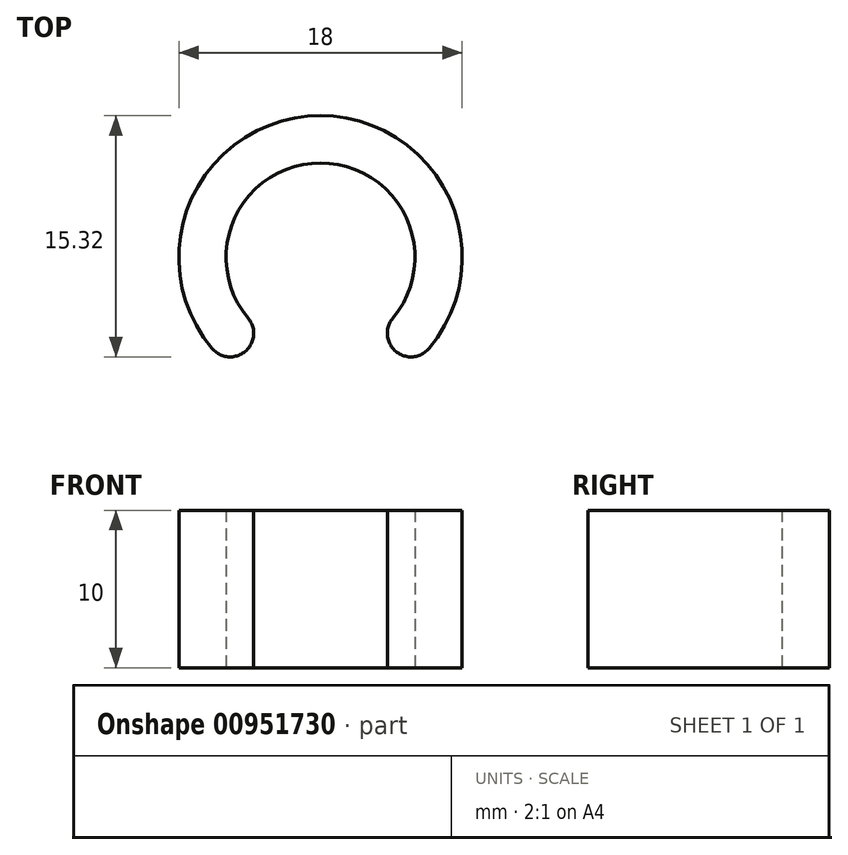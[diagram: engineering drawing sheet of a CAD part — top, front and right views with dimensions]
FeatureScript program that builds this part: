
annotation { "Feature Type Name" : "Feature", "Feature Type Description" : "" }
export const myFeature = defineFeature(function(context is Context, id is Id, definition is map)
    precondition{}
    {
        {
            var Q0;
            Q0=qCreatedBy(makeId("Top.planeOp"),FACE);
            var sketch = newSketch(context, id + "F0", { "sketchPlane" : qUnion([Q0])});
            skArc(sketch, "E0", {"start": v(6.9, -5.79) * mm, "mid": v(0, 9) * mm, "end": v(-6.9, -5.79) * mm});
            skArc(sketch, "E1", {"start": v(4.6, -3.86) * mm, "mid": v(0, 6) * mm, "end": v(-4.6, -3.86) * mm});
            skLineSegment(sketch, "E2", {"start": v(0, 0) * mm, "end": v(0, -9) * mm, "construction": true});
            skLineSegment(sketch, "E3", {"start": v(0, 0) * mm, "end": v(-6.9, -5.79) * mm, "construction": true});
            skLineSegment(sketch, "E4.MirrorCS", {"start": v(0, 0) * mm, "end": v(6.9, -5.79) * mm, "construction": true});
            skPoint(sketch, "E5", {"position": v(-4.6, -3.86) * mm});
            skPoint(sketch, "E6", {"position": v(4.6, -3.86) * mm});
            skArc(sketch, "E7", {"start": v(-6.9, -5.79) * mm, "mid": v(-4.78, -5.97) * mm, "end": v(-4.6, -3.86) * mm});
            skArc(sketch, "E8", {"start": v(6.9, -5.79) * mm, "mid": v(4.78, -5.97) * mm, "end": v(4.6, -3.86) * mm});
            skLineSegment(sketch, "E9", {"start": v(-4.25, -4.82) * mm, "end": v(-4.25, 4.24) * mm, "construction": true});
            skSolve(sketch);
        }
        {
            var Q0;
            Q0=qSketchRegion(id+"F0",true);
            extrude(context, id + "F1", {"entities" : qUnion([Q0]), "depth" : 10 * mm});
        }
    });
